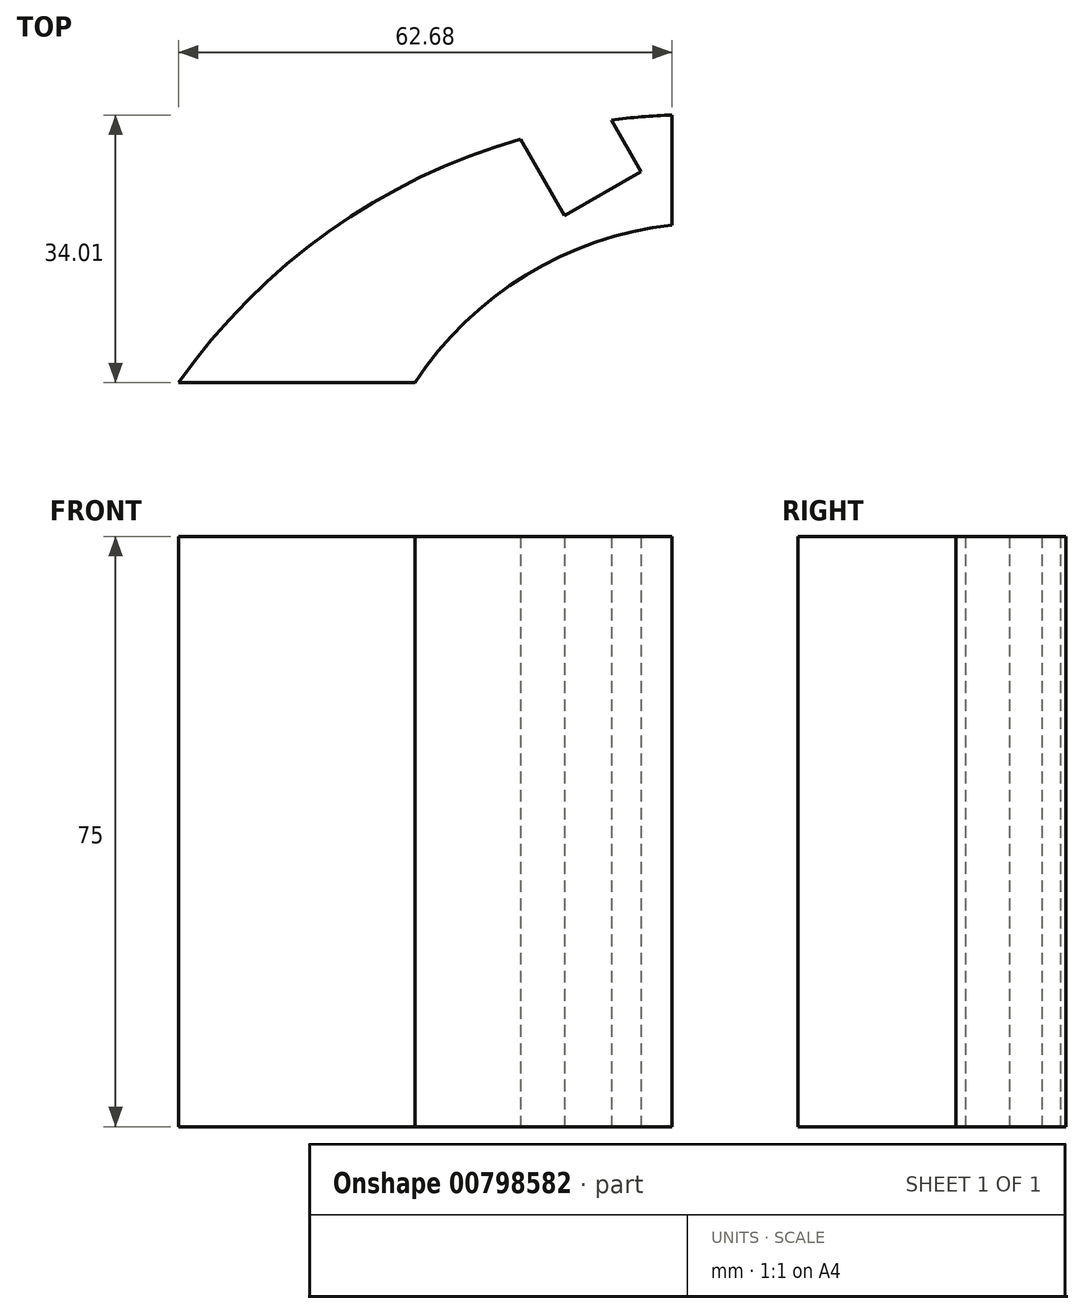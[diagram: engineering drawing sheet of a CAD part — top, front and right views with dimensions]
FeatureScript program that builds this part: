
annotation { "Feature Type Name" : "Feature", "Feature Type Description" : "" }
export const myFeature = defineFeature(function(context is Context, id is Id, definition is map)
    precondition{}
    {
        {
            var Q0;
            Q0=qCreatedBy(makeId("Top.planeOp"),FACE);
            var sketch = newSketch(context, id + "F0", { "sketchPlane" : qUnion([Q0])});
            skArc(sketch, "E0", {"start": v(31.33, 17.01) * mm, "mid": v(26.67, 16.71) * mm, "end": v(22.04, 16.14) * mm});
            skArc(sketch, "E1", {"start": v(31.33, 3.04) * mm, "mid": v(12.76, -3.33) * mm, "end": v(-1.33, -17) * mm});
            skLineSegment(sketch, "E2", {"start": v(-31.35, -17) * mm, "end": v(-1.33, -17) * mm});
            skLineSegment(sketch, "E3", {"start": v(31.33, 17.01) * mm, "end": v(31.33, 3.04) * mm});
            skLineSegment(sketch, "E4", {"start": v(13.59, 14.38) * mm, "end": v(19, 5) * mm, "construction": true});
            skLineSegment(sketch, "E5", {"start": v(17.7, 4.25) * mm, "end": v(19, 5) * mm});
            skLineSegment(sketch, "E6", {"start": v(26.1, 9.1) * mm, "end": v(22.04, 16.14) * mm, "construction": true});
            skLineSegment(sketch, "E7", {"start": v(12.1, 13.96) * mm, "end": v(17.7, 4.25) * mm});
            skLineSegment(sketch, "E8", {"start": v(23.64, 16.37) * mm, "end": v(27.4, 9.85) * mm});
            skLineSegment(sketch, "E9", {"start": v(19, 5) * mm, "end": v(26.1, 9.1) * mm});
            skLineSegment(sketch, "E10", {"start": v(26.1, 9.1) * mm, "end": v(27.4, 9.85) * mm});
            skArc(sketch, "E11.trimOffspring", {"start": v(13.59, 14.38) * mm, "mid": v(-11.65, 2.66) * mm, "end": v(-31.35, -17) * mm});
            skSolve(sketch);
        }
        {
            var Q0;
            Q0=makeQuery(id+"F0.imprint","IMPRINT",FACE,{"disambiguationData":[TD([[makeQuery(id+"F0.imprint","IMPRINT",EDGE,{"derivedFrom":sQuery(id+"F0.wireOp",EDGE,"E1")}),-1.0]])]});
            extrude(context, id + "F1", {"entities" : qUnion([Q0]), "endBound" : BoundingType.SYMMETRIC, "depth" : 75 * mm, "offsetDistance" : 25 * mm});
        }
    });
